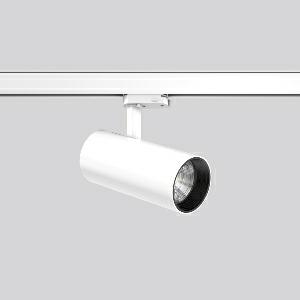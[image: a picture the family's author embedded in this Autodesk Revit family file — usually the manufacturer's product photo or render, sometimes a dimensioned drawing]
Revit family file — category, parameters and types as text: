
# Revit family: deecos_s_mini_742199_002_4fad
name_source: partatom
category: Lighting Fixtures
units: mm (PartAtom-declared; Revit-internal decimal feet)

## family parameters
Cut with Voids When Loaded = No
Host = Face
Light Source = No
Part Type = Normal
Room Calculation Point = No
Round Connector Dimension = Use Diameter
Shared = No

## types (1)
- DEECOS S mini (1 x LED Modul 930, 2100 lm, 3000)
    Apparent Load = 20 VA
    Approval mark = CE
    CIE Flux Codes = 96 100 100 100 100
    Color Rendering = 90
    Color Temperature = 3000
    Default Elevation = 1800 mm
    Description = Series: DEECOS S mini
LED surface-mounted projector in modern design with no visible cooling ribs. Housing: die-cast aluminium, powder-coated. Rotation range: 356°. Swivel range: 90°. Black plastic ring and recessed LED to prevent glare from the side. Optical assembly with lens made of plastic (polycarbonate) for the best homogeneous light distribution - can be changed without tools. Best colour rendering index Ra>90. With multi adaptor for 3-circuit tracks 230 V. Suitable for Track on ceiling, Wall track. High quality converter without flickering and stroboscopic effect. The following accessories can be mounted without use of tools: interchangeable lenses, decorative glasses, honeycomb louvre, clear and frosted diffusers, white interchangeable plastic ring. 
Colour: traffic white, matt (RAL 9016)
Diameter: 87 mm
Height: 214 mm
Lamp: LED
Socket: without socket
Colour temperature: 3000K
Colour rendering index (CRI): 92
System power: 20 W
Rated luminous flux: 2100 lm
Luminous efficiency: 105 lm/W
Control gear: Regulated power supply
Protection class: I
Type of protection: IP 20
    Height = 214 mm
    Lamp = 1 x LED Modul 930
    Lamp Light Flux = 2100 lm
    Lamp count = 1
    Length = 87 mm
    Lifetime = 50000 h
    Luminous efficacy = 105 lm/W
    Manufacturer = RZB
    ModVariant = No
    Model = 742199.002
    Mounting Place = Ceiling
    Mounting Type = Rail mounted
    Number of Poles = 1
    OnlyDefault = Yes
    Power Factor = 1
    Product Name = DEECOS S mini
    Product group = Track mounted projectors
    ProductGroupID = 301
    Protection Class = Protection class I
    Protection Degree = IP 20
    RLX_Detail_Level = 1
    RLX_Emergency_Light_Flux = 0 lm
    RLX_Emergency_Type = 0
    RLX_Emergency_Type_DB = No
    RlxData = <blob elided: 35333 chars, md5=55090a7f>
    Socket = socket
    Standby Power = 0 W
    System Light Flux = 2100 lm
    System Power = 20 W
    Type Comments = Product without accessories
    Type Image = 741930.002.jpg
    URL = http://relux.com
    VarID = ---
    Voltage = 230 V
    Voltage Range = 220-240 V
    Weight = 0.00 kg
    Width = 0 mm  [stored 0 ft]

note: [stored X ft] marks values corroborated as IEEE doubles in the binary element streams (Revit-internal decimal feet)

## geometry (parser evidence)
native form markers: Blend x4, Sweep x12
no freeform markers — native parametric forms only
